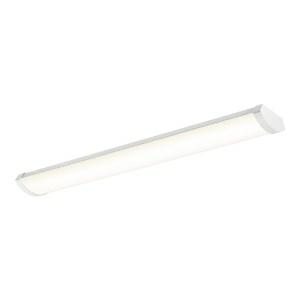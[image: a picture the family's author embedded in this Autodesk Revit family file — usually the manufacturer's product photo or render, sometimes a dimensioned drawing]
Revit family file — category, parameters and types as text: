
# Revit family: ledlinear-e_cl12-40w-4000-wh_542005039800
name_source: partatom
category: Leuchten
revit_build: Autodesk Revit 2016 (Build: 20190508_0715(x64)
units: mm (PartAtom-declared; Revit-internal decimal feet)

## family parameters
Basisbauteil = Fläche
Beim Laden mit Abzugskörper schneiden = Nein
Bemaßung runder Anschluss = Durchmesser verwenden
Gemeinsam genutzt = Nein
Lichtquelle = Nein
Raumberechnungspunkt = Nein
Teiletyp = Normal

## types (1)
- LEDLinear-E CL12-40W-4000-WH (1 x LED, 4720 lm)
    Approval mark = CE
    Beschreibung = Easy to install LED linear solution. Elegant but sturdy design: IP44 and IK06. Comfortable light due to opal diffusor. Central or side power connection. Motion and daylight sensor accessory available.
    CIE Flux Codes = 44 74 91 95 100
    Control Gear = Electronic ballast
    Height = 75 mm
    Hersteller = OPPLE
    Lamp Light Flux = 4720 lm
    Lamp count = 1
    Lampe = 1 x LED
    Length = 180 mm  [stored 0.590551 ft]
    Luminous efficacy = 118 lm/W
    ModVariant = Nein
    Modell = 542005039800
    Mounting Place = Ceiling
    Mounting Type = Surface mounted
    Number of Poles = 1
    OnlyDefault = Ja
    Power Factor = 1
    Product Name = LEDLinear-E CL12-40W-4000-WH
    Product group = Linear EcoMax
    ProductGroupID = 303
    Protection Class = Protection class I
    Protection Degree = IP 44
    RLX_Detail_Level = 1
    RlxData = <blob elided: 95381 chars, md5=6da6587c>
    Scheinlast = 40 VA
    Socket = socket
    Standby Power = 0 W
    System Light Flux = 4720 lm
    System Power = 40 W
    Typenbild = 542005039800.jpg
    Typenkommentare = Product without accessories
    URL = http://relux.com
    VarID = ---
    Voltage = 0 V
    Vorgabe-Ansicht = 1800 mm
    Weight = 0.00 kg
    Width = 1200 mm

note: [stored X ft] marks values corroborated as IEEE doubles in the binary element streams (Revit-internal decimal feet)

## geometry (parser evidence)
native form markers: Blend x4, Sweep x14
no freeform markers — native parametric forms only
